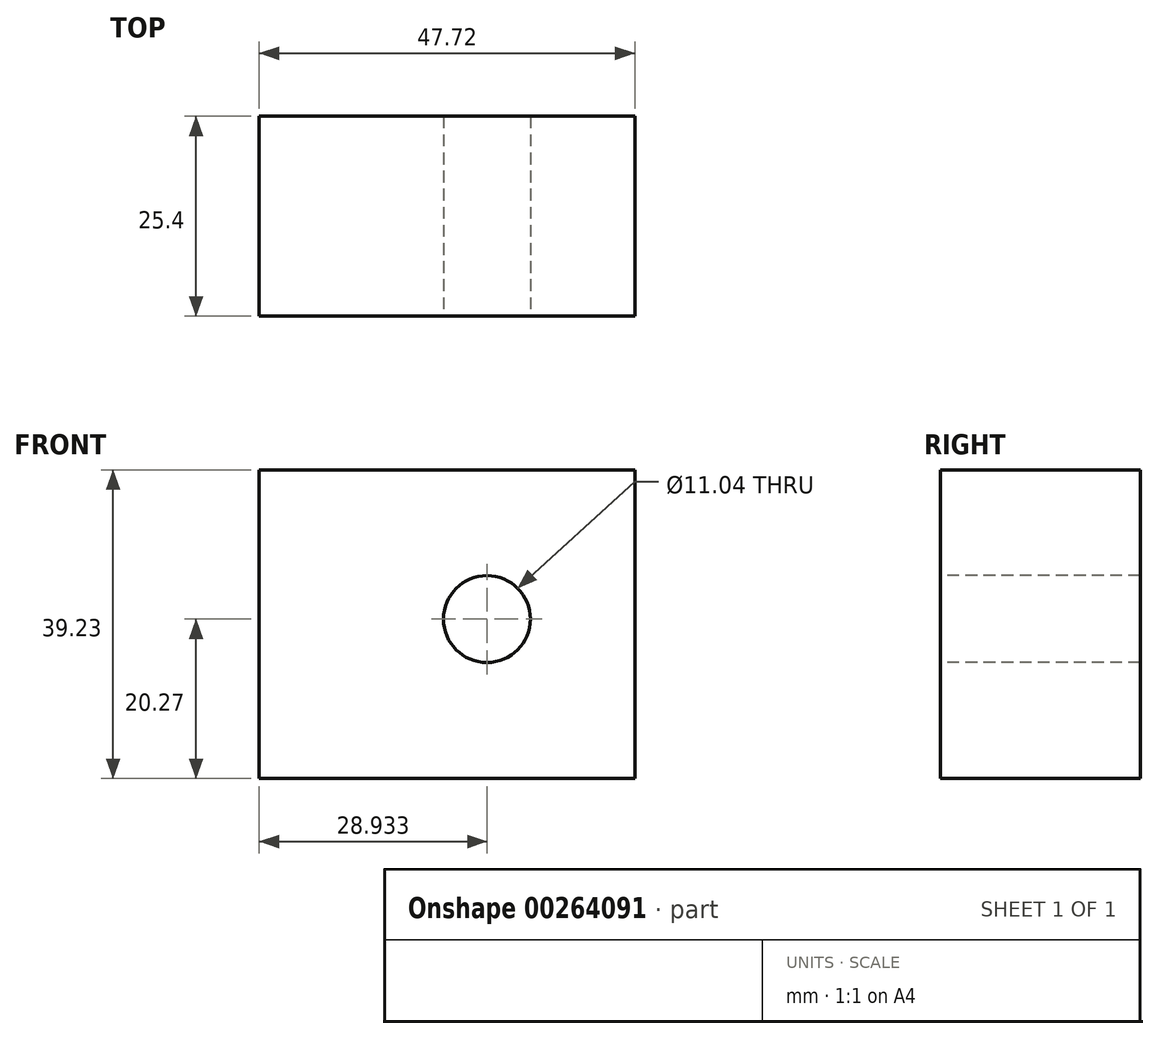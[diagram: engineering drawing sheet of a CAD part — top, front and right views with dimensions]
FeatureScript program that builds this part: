
annotation { "Feature Type Name" : "Feature", "Feature Type Description" : "" }
export const myFeature = defineFeature(function(context is Context, id is Id, definition is map)
    precondition{}
    {
        {
            var Q0;
            Q0=qCreatedBy(makeId("Front.planeOp"),FACE);
            var sketch = newSketch(context, id + "F0", { "sketchPlane" : qUnion([Q0])});
            skLineSegment(sketch, "E0.bottom", {"start": v(0, 0) * mm, "end": v(47.72, 0) * mm});
            skLineSegment(sketch, "E0.top", {"start": v(0, 39.23) * mm, "end": v(47.72, 39.23) * mm});
            skLineSegment(sketch, "E0.left", {"start": v(0, 0) * mm, "end": v(0, 39.23) * mm});
            skLineSegment(sketch, "E0.right", {"start": v(47.72, 0) * mm, "end": v(47.72, 39.23) * mm});
            skSolve(sketch);
        }
        {
            var Q0;
            Q0=makeQuery(id+"F0.imprint","IMPRINT",FACE,{"disambiguationData":[TD([[makeQuery(id+"F0.imprint","IMPRINT",EDGE,{"derivedFrom":sQuery(id+"F0.wireOp",EDGE,"E0.bottom")}),1.0]])]});
            extrude(context, id + "F1", {"entities" : qUnion([Q0]), "depth" : 25.4 * mm});
        }
        {
            var Q0;
            Q0=makeQuery(id+"F1.opExtrude","CAP_FACE",FACE,{"disambiguationData":[OSD([sQuery(id+"F0.wireOp",EDGE,"E0.bottom"),sQuery(id+"F0.wireOp",EDGE,"E0.top"),sQuery(id+"F0.wireOp",EDGE,"E0.left"),sQuery(id+"F0.wireOp",EDGE,"E0.right")])],"isStart":false});
            var sketch = newSketch(context, id + "F2", { "sketchPlane" : qUnion([Q0])});
            skCircle(sketch, "E1", {"center": v(28.93, 20.27) * mm, "radius": 5.52 * mm});
            skSolve(sketch);
        }
        {
            var Q0;
            Q0=makeQuery(id+"F2.imprint","IMPRINT",FACE,{"disambiguationData":[TD([[makeQuery(id+"F2.imprint","IMPRINT",EDGE,{"derivedFrom":sQuery(id+"F2.wireOp",EDGE,"E1")}),1.0]])]});
            extrude(context, id + "F3", {"entities" : qUnion([Q0]), "operationType" : NewBodyOperationType.REMOVE, "endBound" : BoundingType.UP_TO_NEXT, "oppositeDirection" : true, "depth" : 25.4 * mm});
        }
    });
